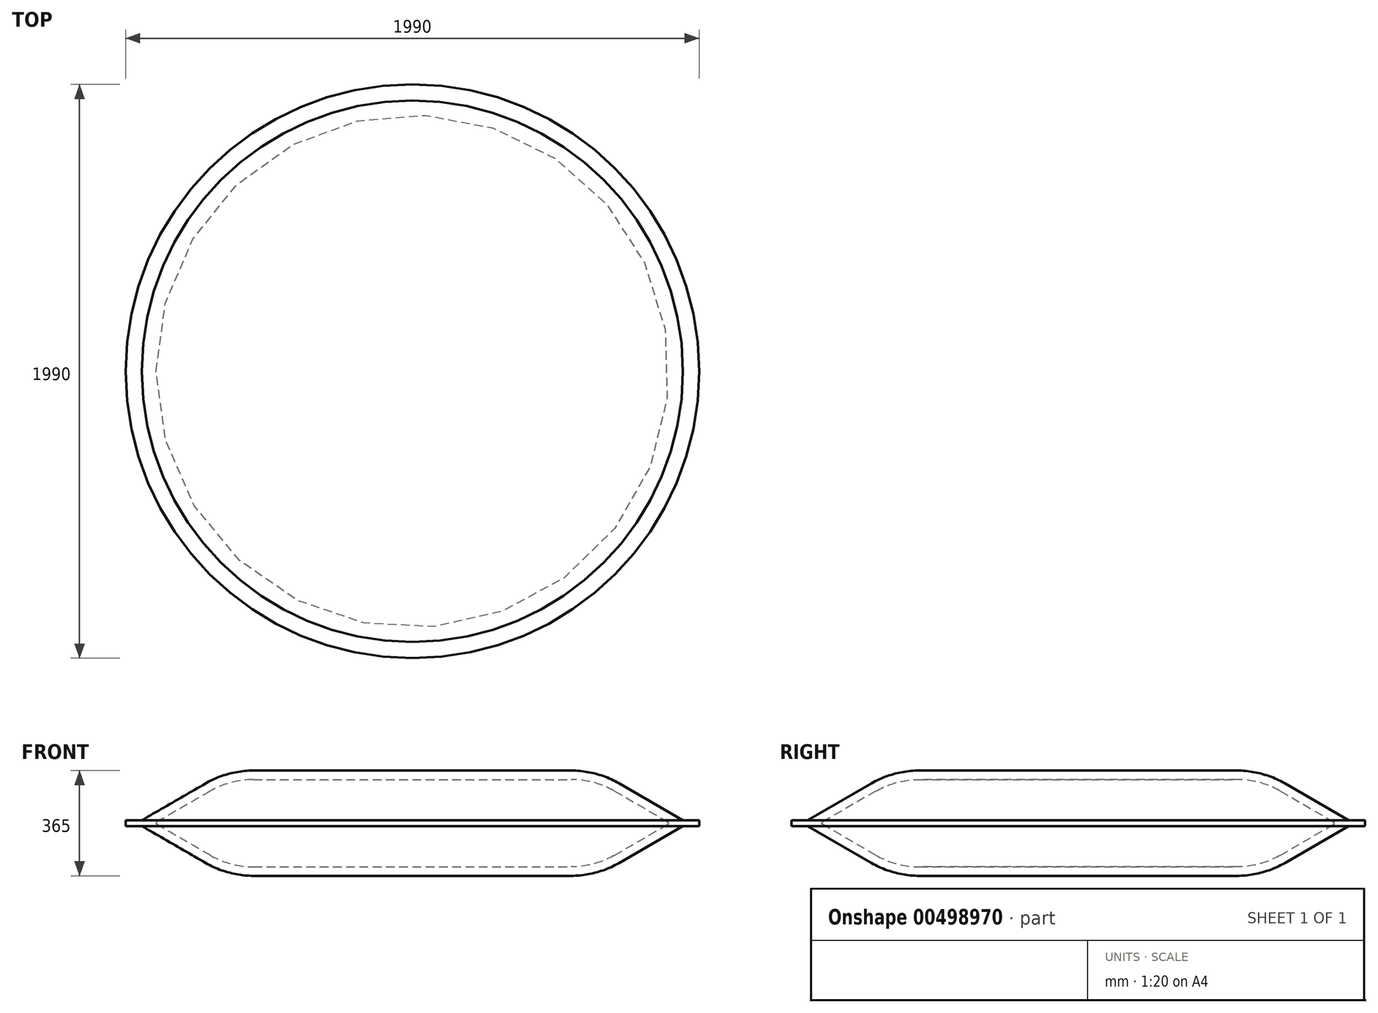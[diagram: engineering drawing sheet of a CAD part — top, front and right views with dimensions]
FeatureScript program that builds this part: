
annotation { "Feature Type Name" : "Feature", "Feature Type Description" : "" }
export const myFeature = defineFeature(function(context is Context, id is Id, definition is map)
    precondition{}
    {
        {
            var Q0;
            Q0=qCreatedBy(makeId("Front.planeOp"),FACE);
            var sketch = newSketch(context, id + "F0", { "sketchPlane" : qUnion([Q0])});
            skLineSegment(sketch, "E0", {"start": v(0, 0) * mm, "end": v(0, 631.16) * mm, "construction": true});
            skLineSegment(sketch, "E1", {"start": v(0, -182.5) * mm, "end": v(-995, -182.5) * mm, "construction": true});
            skLineSegment(sketch, "E2", {"start": v(0, 0) * mm, "end": v(-995, 0) * mm, "construction": true});
            skLineSegment(sketch, "E3", {"start": v(-995, 0) * mm, "end": v(-995, -10) * mm});
            skLineSegment(sketch, "E4", {"start": v(0, -182.5) * mm, "end": v(-551.3, -182.5) * mm});
            skLineSegment(sketch, "E5", {"start": v(-995, -10) * mm, "end": v(-938.78, -10) * mm});
            skLineSegment(sketch, "E6", {"start": v(-716.8, -138.15) * mm, "end": v(-938.78, -10) * mm});
            skPoint(sketch, "E7.visualSharp", {"position": v(-640, -182.5) * mm});
            skArc(sketch, "E7.filletArc", {"start": v(-716.8, -138.15) * mm, "mid": v(-636.98, -171.22) * mm, "end": v(-551.3, -182.5) * mm});
            skLineSegment(sketch, "E8", {"start": v(-886.6, -4.33) * mm, "end": v(-701.3, -111.3) * mm});
            skLineSegment(sketch, "E9", {"start": v(-551.3, -151.5) * mm, "end": v(0, -151.5) * mm});
            skLineSegment(sketch, "E10", {"start": v(0, 0) * mm, "end": v(0, -333.88) * mm, "construction": true});
            skArc(sketch, "E11.filletArc", {"start": v(-701.3, -111.3) * mm, "mid": v(-628.95, -141.28) * mm, "end": v(-551.3, -151.5) * mm});
            skLineSegment(sketch, "E12.MirrorCS", {"start": v(-995, 0) * mm, "end": v(-995, 10) * mm});
            skLineSegment(sketch, "E13.MirrorCS", {"start": v(0, 182.5) * mm, "end": v(-551.3, 182.5) * mm});
            skLineSegment(sketch, "E14.MirrorCS", {"start": v(-551.3, 151.5) * mm, "end": v(0, 151.5) * mm});
            skLineSegment(sketch, "E15.MirrorCS", {"start": v(-886.6, 4.33) * mm, "end": v(-701.3, 111.3) * mm});
            skArc(sketch, "E16.MirrorCS", {"start": v(-716.8, 138.15) * mm, "mid": v(-636.98, 171.22) * mm, "end": v(-551.3, 182.5) * mm});
            skPoint(sketch, "E17.MirrorP", {"position": v(-640, 182.5) * mm});
            skLineSegment(sketch, "E18.MirrorCS", {"start": v(-716.8, 138.15) * mm, "end": v(-938.78, 10) * mm});
            skLineSegment(sketch, "E19.MirrorCS", {"start": v(-995, 10) * mm, "end": v(-938.78, 10) * mm});
            skLineSegment(sketch, "E20.MirrorCS", {"start": v(0, 182.5) * mm, "end": v(-995, 182.5) * mm, "construction": true});
            skArc(sketch, "E21.MirrorCS", {"start": v(-701.3, 111.3) * mm, "mid": v(-628.95, 141.28) * mm, "end": v(-551.3, 151.5) * mm});
            skPoint(sketch, "E22.visualSharp", {"position": v(-894.1, 0) * mm});
            skArc(sketch, "E22.filletArc", {"start": v(-886.6, 4.33) * mm, "mid": v(-889.1, 0) * mm, "end": v(-886.6, -4.33) * mm});
            skLineSegment(sketch, "E23", {"start": v(0, 182.5) * mm, "end": v(0, 151.5) * mm});
            skLineSegment(sketch, "E24", {"start": v(0, -182.5) * mm, "end": v(0, -151.5) * mm});
            skSolve(sketch);
        }
        {
            var Q0;
            Q0=qCreatedBy(makeId("Right.planeOp"),FACE);
            var sketch = newSketch(context, id + "F1", { "sketchPlane" : qUnion([Q0])});
            skLineSegment(sketch, "E25", {"start": v(0, 0) * mm, "end": v(0, 468.26) * mm});
            skSolve(sketch);
        }
        {
            var Q0;
            Q0 = qSketchRegion(id + "F0", true);
            var Q1;
            Q1=sQuery(id+"F1.wireOp",EDGE,"E25");
            revolve(context, id + "F2", {"entities" : qUnion([Q0]), "axis" : qUnion([Q1]), "revolveType" : RevolveType.ONE_DIRECTION, "angle" : 360 * degree});
        }
    });
